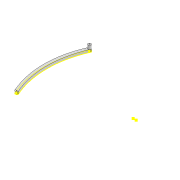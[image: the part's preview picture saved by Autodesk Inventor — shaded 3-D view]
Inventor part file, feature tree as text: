
AUTODESK INVENTOR PART (.ipt)
format: ipt  version: 2022 (Build 260153000, 153)  size: 123,392 bytes
history: native  units: mm
features: sketch x3, extrude x2, projected_geometry x2, fillet x1
ambient origin geometry x8: Origin, YZ Plane, XZ Plane, XY Plane, X Axis, Y Axis, Z Axis, Center Point
bodies: Solid1 (feature_tree)
feature tree (8):
  extrude  "Extrusion1"  Depth=10.0mm
  extrude  "Extrusion2"  Depth=8.0mm
  sketch  "Sketch3"  dims[d12=10.0mm d13=12.0mm d14=0.0mm d18=300.0mm d19=300.0mm d20=4.0mm]
  fillet  "Fillet1"  Radius=8.0mm
  sketch  "Sketch1"  dims[d0=244.795mm d1=10.0mm]
  sketch  "Sketch2"  dims[d2=3.0mm d3=3.0mm d4=8.0mm d5=0.0mm]
  projected_geometry  "Projected Loop1"
  projected_geometry  "Projected Loop2"
